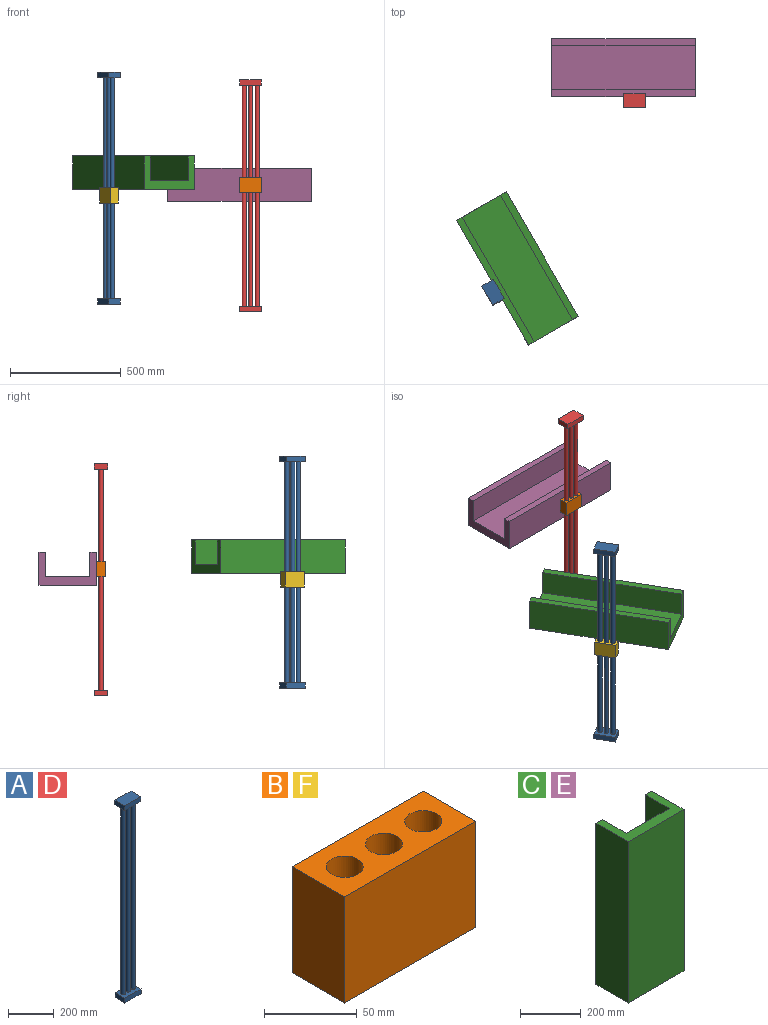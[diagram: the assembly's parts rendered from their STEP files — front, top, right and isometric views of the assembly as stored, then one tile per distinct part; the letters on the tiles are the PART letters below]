
ASSEMBLY  parts=6 mates=7
PART A: 15 faces, bbox 100x60.8x1050 mm
  f0: plane 60x25mm, normal (-1,0,0), area 1500mm2, adj f1,f3,f4,f5
  f1: plane 100x25mm, normal (0,-1,0), area 2500mm2, adj f0,f2,f4,f5
  f2: plane 60x25mm, normal (1,0,0), area 1500mm2, adj f1,f3,f4,f5
  f3: plane 100x25mm, normal (0,1,0), area 2500mm2, adj f0,f2,f4,f5
  f4: plane 100x60mm, normal (0,0,1), area 5057.5mm2, adj f0,f1,f2,f3,f6,f7,f8
  f5: plane 100x60mm, normal (0,0,-1), area 6000mm2, adj f0,f1,f2,f3
  f6: cylinder r=10mm len=1000mm, axis (0,0,-1), area 62831.9mm2, adj f4,f14
  f7: cylinder r=10mm len=1000mm, axis (0,0,-1), area 62831.9mm2, adj f4,f14
  f8: cylinder r=10mm len=1000mm, axis (0,0,-1), area 62831.9mm2, adj f4,f14
  f9: plane 98.95x25mm, normal (0,1,0), area 2473.6mm2, adj f10,f12,f13,f14
  f10: plane 60.76x25mm, normal (-1,0,0), area 1519.1mm2, adj f9,f11,f13,f14
  f11: plane 98.95x25mm, normal (0,-1,0), area 2473.6mm2, adj f10,f12,f13,f14
  f12: plane 60.76x25mm, normal (1,0,0), area 1519.1mm2, adj f9,f11,f13,f14
  f13: plane 98.95x60.76mm, normal (0,0,1), area 6012.3mm2, adj f9,f10,f11,f12
  f14: plane 98.95x60.76mm, normal (0,0,-1), area 5069.8mm2, adj f6,f7,f8,f9,f10,f11,f12
PART B: 9 faces, bbox 100x40x70 mm
  f0: plane 70x40mm, normal (-1,0,0), area 2800mm2, adj f1,f5,f7,f8
  f1: plane 100x70mm, normal (0,-1,0), area 7000mm2, adj f0,f2,f7,f8
  f2: plane 70x40mm, normal (1,0,0), area 2800mm2, adj f1,f5,f7,f8
  f3: cylinder r=10mm len=70mm, axis (0,0,-1), area 4398.2mm2, adj f7,f8
  f4: cylinder r=10mm len=70mm, axis (0,0,-1), area 4398.2mm2, adj f7,f8
  f5: plane 100x70mm, normal (0,1,0), area 7000mm2, adj f0,f2,f7,f8
  f6: cylinder r=10mm len=70mm, axis (0,0,-1), area 4398.2mm2, adj f7,f8
  f7: plane 100x40mm, normal (0,0,1), area 3057.5mm2, adj f0,f1,f2,f3,f4,f5,f6
  f8: plane 100x40mm, normal (0,0,-1), area 3057.5mm2, adj f0,f1,f2,f3,f4,f5,f6
PART C: 10 faces, bbox 260x150x650 mm
  f0: plane 650x150mm, normal (-1,0,0), area 97500mm2, adj f1,f7,f8,f9
  f1: plane 650x260mm, normal (0,-1,0), area 169000mm2, adj f0,f2,f8,f9
  f2: plane 650x150mm, normal (1,0,0), area 97500mm2, adj f1,f3,f8,f9
  f3: plane 650x30mm, normal (0,1,0), area 19500mm2, adj f2,f4,f8,f9
  f4: plane 650x110.98mm, normal (-1,0,0), area 72139.2mm2, adj f3,f5,f8,f9
  f5: plane 650x200mm, normal (0,1,0), area 130000mm2, adj f4,f6,f8,f9
  f6: plane 650x110.98mm, normal (1,0,0), area 72139.2mm2, adj f5,f7,f8,f9
  f7: plane 650x30mm, normal (0,1,0), area 19500mm2, adj f0,f6,f8,f9
  f8: plane 260x150mm, normal (0,0,1), area 16803.3mm2, adj f0,f1,f2,f3,f4,f5,f6,f7
  f9: plane 260x150mm, normal (0,0,-1), area 16803.3mm2, adj f0,f1,f2,f3,f4,f5,f6,f7
PART D: same geometry as A
PART E: same geometry as C
PART F: same geometry as B
PLACE A rot(axis=(0,0,-1),60deg) t=(-575.74,-297.71,-304.92)mm
PLACE B t=(65.76,520.67,200.25)mm
PLACE C rot(axis=(0.19,-0.69,-0.69),158.9deg) t=(-139.53,-433.24,215.95)mm
PLACE D t=(65.76,510.67,-339.13)mm
PLACE E rot(axis=(0.58,-0.58,-0.58),120deg) t=(390.76,820.67,160.25)mm
PLACE F rot(axis=(0,0,-1),60deg) t=(-567.08,-292.71,152.94)mm
MATE planar C.f2 <-> F.f5  axis (-0.87,-0.5,0) through (-527.2,-281.78,290.95)mm
MATE slider B.f3 <-> D.f7  axis (0,0,1) through (115.76,540.67,270.25)mm
MATE planar E.f2 <-> B.f5  axis (0,-1,0) through (65.76,560.67,235.25)mm
MATE slider F.f3 <-> A.f7  axis (0,0,1) through (-524.76,-326.01,222.94)mm
MATE cylindrical B.f3 <-> D.f7  axis (0,0,-1) through (115.76,540.67,200.25)mm
MATE planar E.f2 <-> B.f5  axis (0,-1,0) through (65.76,560.67,235.25)mm
MATE cylindrical F.f3 <-> A.f7  axis (0,0,-1) through (-524.76,-326.01,152.94)mm
